# Revit family: MTXTYP007
name_source: partatom
category: Furniture
units: mm (PartAtom-declared; Revit-internal decimal feet)

## family parameters
Always vertical = Yes
Cut with Voids When Loaded = No
OmniClass Number = 23.40.20.00
OmniClass Title = General Furniture and Specialties
Render Appearance Source = Family Geometry
Room Calculation Point = No
Shared = No
Work Plane-Based = No

## types (1)
- MTXTYP007
    Cost = 42202 $
    Default Elevation = 0 mm  [stored 0 ft]
    Description = 2 x 24 Led Task Light, W/ Dimmer & Transformer, 1 x 43 in. Electrical Jumper  (Pt 24 & Vt32), 1 x Matrix Black Duplex Outlet - Line 1, 1 x Matrix Black Duplex Outlet - Line 2, 1 x Matrix Black Duplex Outlet - Line 3, 1 x Matrix Black Duplex Outlet - Line 4 - Dedicated, 1 x 21 in. Electrical Jumper  (Extended Panel To Panel), 1 x Single Powerway Assembly - 30W - 8 wire, 4 circuit, 1 x Single Powerway Assembly - 36W - 8 wire, 4 circuit, 1 x LH Receptacle Mounted Base Infeed - 72L - 8 Wire, 4 Circuit, 1 x Universal 8 Wire 4 Cir I Connector, 4 x Volker Cube w/Casters - 18x18x18, 1 x Stack On Frame - 16H x 36W, 2 x Dual Electrical Tile - 8H X 30W, 1 x Dual Electrical Tile - 8H X 36W, 2 x Tackable Acoustical Tile - 24H x 30W, 2 x Tackable Acoustical Tile - 32H x 30W, 2 x Tackable Acoustical Tile - 32H x 36W, 2 x Tackable Acoustical Tile - 40H x 36W, 2 x Tackable Acoustical Tile - 48H x 24W, 2 x Tackable Acoustical Tile - 48H x 42W, 1 x Tackable Acoustical Tile - 56H x 36W, 3 x Tackable Acoustical Tile - 64H x 36W, 1 x 3-Way  90 Degree Connector - Linear Trim - 66H, 1 x Frame End Cap - Linear Trim - 42H, 1 x Frame End Cap - Linear Trim - 50H, 1 x Panel Frame - Linear Trim - 34H x 36W, 1 x Panel Frame - Linear Trim - 42H x 36W, 1 x Panel Frame - Linear Trim - 50H x 24W, 1 x Panel Frame - Linear Trim - 50H x 42W, 1 x Panel Frame - Linear Trim - 66H x 30W, 2 x Panel Frame - Linear Trim - 66H x 36W, 1 x MTX Gallery Panel EOR DBL-50H x 60W Horz, 2 x Straight HiLo - Linear Trim - 16H, 1 x Straight HiLo - Linear Trim - 24H, 1 x Back Glass Tile - Linear Trim - 16H x 36W, 1 x Front Glass Tile - Linear Trim - 16H x 36W, 2 x Cushion for Credenza - 18D x 42W, 2 x Type C Flipper Unit - Laminate Face - 30W, 2 x Rectangular - 2mm Edge - 30D x 72W, 2 x A-Leg - 2.5 x 2.5 Post - 27H - 30 Depth, 2 x Regular Cantilever - Left Hand - 30D, 2 x Regular Cantilever - Right Hand - 30D, 2 x Cbx Full Depth Floor Bookcase 18dx28hx30w, 2 x Cbx Full Depth Lat Bf 18dx21hx42w, 1 x Cbx Wardrobe Bf Cd Lh 24dx50hx24w, 1 x Cbx Wardrobe Bf Cd Rh 24dx50hx24w, 1 x Cbx Rectangular Ro For 29h Post Leg 30dx60w
    Exported From CET Designer = Yes
    Manufacturer = AIS
    Model = A-LEDTL-61024
    Show MTXTYP007 = Yes
    VisibilityIndex = 0

note: [stored X ft] marks values corroborated as IEEE doubles in the binary element streams (Revit-internal decimal feet)

## geometry (parser evidence)
native form markers: Sweep x2
no freeform markers — native parametric forms only
